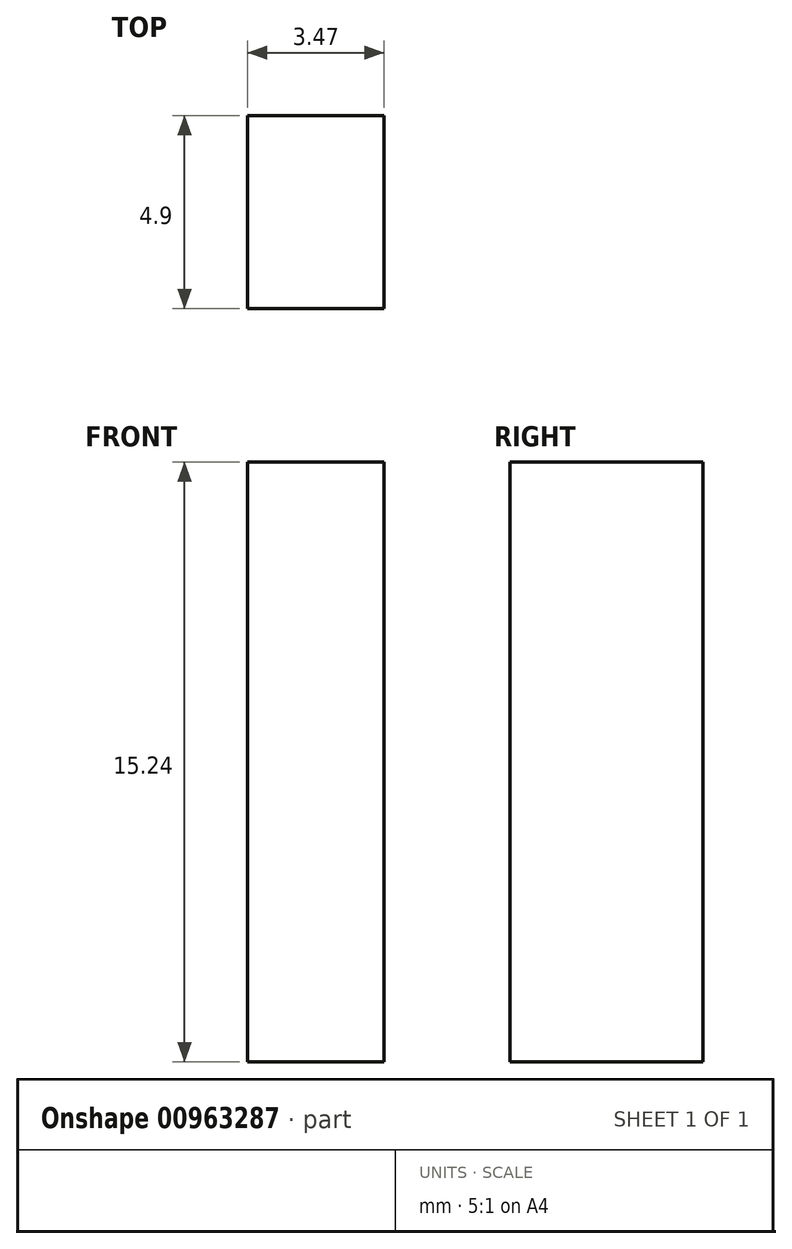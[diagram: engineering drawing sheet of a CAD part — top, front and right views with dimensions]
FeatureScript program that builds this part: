
annotation { "Feature Type Name" : "Feature", "Feature Type Description" : "" }
export const myFeature = defineFeature(function(context is Context, id is Id, definition is map)
    precondition{}
    {
        {
            var Q0;
            Q0=qCreatedBy(makeId("Top.planeOp"),FACE);
            var sketch = newSketch(context, id + "F0", { "sketchPlane" : qUnion([Q0])});
            skLineSegment(sketch, "E0", {"start": v(-12.15, -27.85) * mm, "end": v(-2.15, -27.85) * mm});
            skLineSegment(sketch, "E1", {"start": v(-12.15, 12.15) * mm, "end": v(-2.15, 12.15) * mm});
            skLineSegment(sketch, "E2.bottom", {"start": v(-25, 0) * mm, "end": v(-21.53, 0) * mm});
            skLineSegment(sketch, "E2.top", {"start": v(-25, -4.9) * mm, "end": v(-21.53, -4.9) * mm});
            skLineSegment(sketch, "E2.left", {"start": v(-25, 0) * mm, "end": v(-25, -4.9) * mm});
            skLineSegment(sketch, "E2.right", {"start": v(-21.53, 0) * mm, "end": v(-21.53, -4.9) * mm});
            skArc(sketch, "E3", {"start": v(-12.15, 12.15) * mm, "mid": v(-32.15, -7.85) * mm, "end": v(-12.15, -27.85) * mm});
            skArc(sketch, "E4", {"start": v(-2.15, 12.15) * mm, "mid": v(-4.05, -7.85) * mm, "end": v(-2.15, -27.85) * mm});
            skSolve(sketch);
        }
        {
            var Q0;
            Q0=makeQuery(id+"F0.imprint","IMPRINT",FACE,{"disambiguationData":[TD([[makeQuery(id+"F0.imprint","IMPRINT",EDGE,{"derivedFrom":sQuery(id+"F0.wireOp",EDGE,"E2.bottom")}),-1.0]])]});
            extrude(context, id + "F1", {"entities" : qUnion([Q0]), "depth" : 15.24 * mm, "offsetDistance" : 25.4 * mm});
        }
    });
